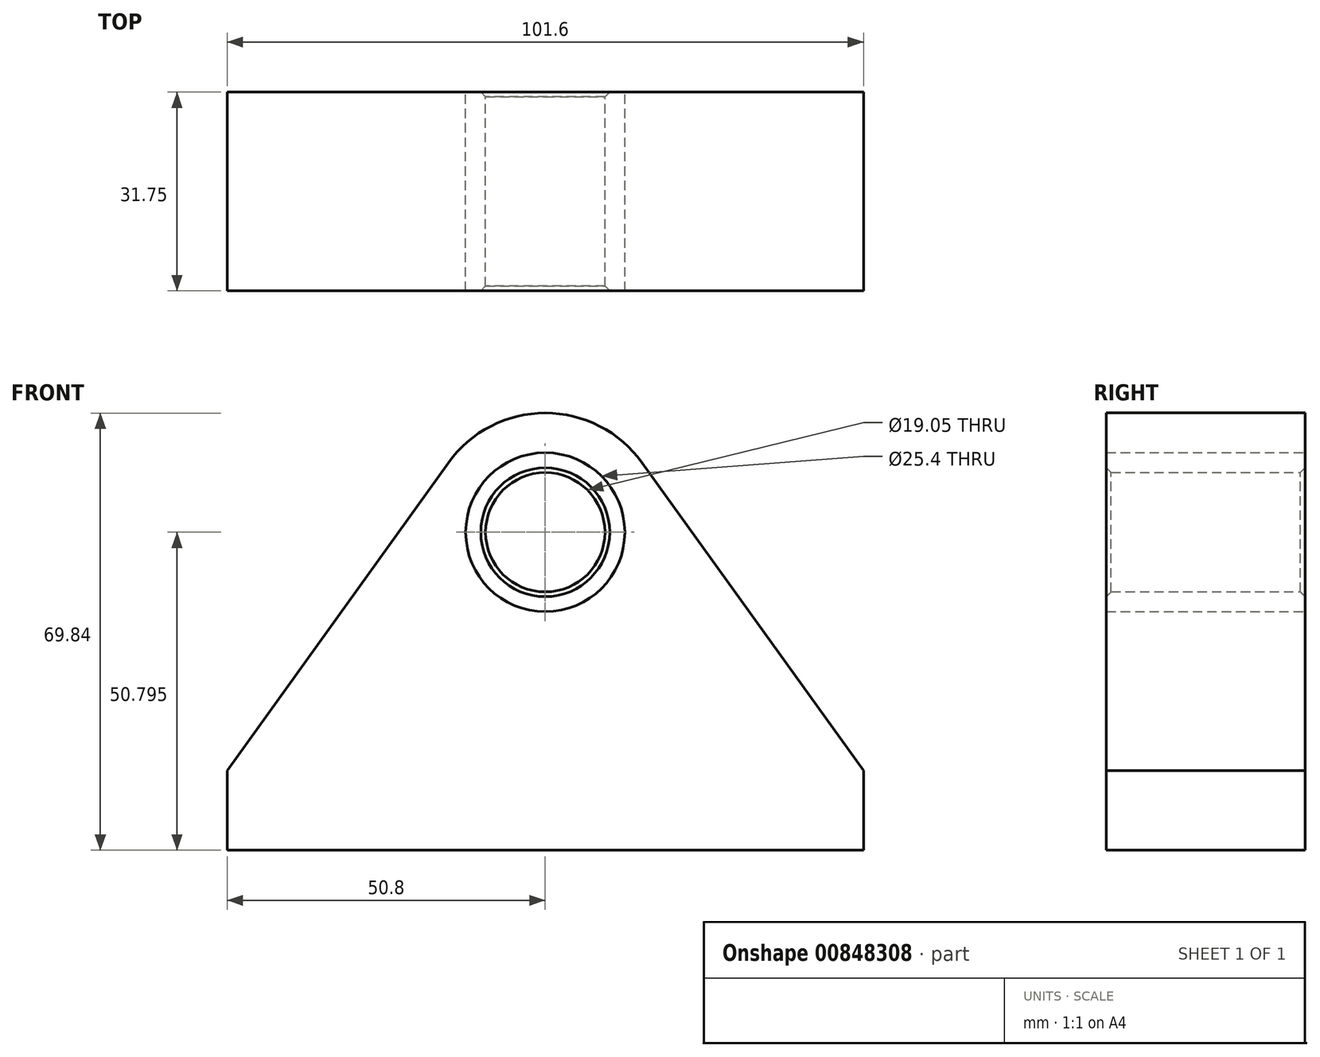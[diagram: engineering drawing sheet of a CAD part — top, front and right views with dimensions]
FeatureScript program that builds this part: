
annotation { "Feature Type Name" : "Feature", "Feature Type Description" : "" }
export const myFeature = defineFeature(function(context is Context, id is Id, definition is map)
    precondition{}
    {
        {
            var Q0;
            Q0=qCreatedBy(makeId("Front.planeOp"),FACE);
            var sketch = newSketch(context, id + "F0", { "sketchPlane" : qUnion([Q0])});
            skLineSegment(sketch, "E0.bottom", {"start": v(-50.8, -34.93) * mm, "end": v(50.8, -34.93) * mm});
            skLineSegment(sketch, "E0.left", {"start": v(-50.8, -34.93) * mm, "end": v(-50.8, -22.23) * mm});
            skLineSegment(sketch, "E0.right", {"start": v(50.8, -34.93) * mm, "end": v(50.8, -22.23) * mm});
            skPoint(sketch, "E0.middle", {"position": v(0, 0) * mm});
            skPoint(sketch, "E1", {"position": v(0, 15.87) * mm});
            skCircle(sketch, "E2", {"center": v(0, 15.87) * mm, "radius": 9.53 * mm});
            skPoint(sketch, "E3", {"position": v(-50.8, -22.23) * mm});
            skLineSegment(sketch, "E4", {"start": v(0, 34.93) * mm, "end": v(0, -34.93) * mm, "construction": true});
            skArc(sketch, "E5", {"start": v(15.48, 26.98) * mm, "mid": v(0, 34.93) * mm, "end": v(-15.48, 26.98) * mm});
            skLineSegment(sketch, "E6", {"start": v(-50.8, -22.23) * mm, "end": v(-15.48, 26.98) * mm});
            skLineSegment(sketch, "E7.MirrorCS", {"start": v(50.8, -22.23) * mm, "end": v(15.48, 26.98) * mm});
            skArc(sketch, "E8.MirrorCS", {"start": v(-15.48, 26.98) * mm, "mid": v(0, 34.93) * mm, "end": v(15.48, 26.98) * mm});
            skPoint(sketch, "E9.orphan", {"position": v(0, -3.18) * mm});
            skPoint(sketch, "E10.orphan", {"position": v(50.8, 34.93) * mm});
            skPoint(sketch, "E11.orphan", {"position": v(-50.8, 34.93) * mm});
            skCircle(sketch, "E12", {"center": v(0, 15.87) * mm, "radius": 12.7 * mm});
            skSolve(sketch);
        }
        {
            var Q0;
            Q0=makeQuery(id+"F0.imprint","IMPRINT",FACE,{"disambiguationData":[TD([[makeQuery(id+"F0.imprint","IMPRINT",EDGE,{"derivedFrom":sQuery(id+"F0.wireOp",EDGE,"E0.bottom")}),1.0]])]});
            extrude(context, id + "F1", {"entities" : qUnion([Q0]), "depth" : 31.75 * mm, "offsetDistance" : 25.4 * mm});
        }
        {
            var Q0;
            Q0=makeQuery(id+"F0.imprint","IMPRINT",FACE,{"disambiguationData":[TD([[makeQuery(id+"F0.imprint","IMPRINT",EDGE,{"derivedFrom":sQuery(id+"F0.wireOp",EDGE,"E2")}),-1.0]])]});
            extrude(context, id + "F2", {"entities" : qUnion([Q0]), "depth" : 31.75 * mm, "offsetDistance" : 25.4 * mm});
        }
        {
            var Q0;
            Q0=makeQuery(id+"F2.opExtrude","CAP_EDGE",EDGE,{"disambiguationData":[OSD([sQuery(id+"F0.wireOp",EDGE,"E2")])],"isStart":false});
            var Q1;
            Q1=makeQuery(id+"F2.opExtrude","CAP_EDGE",EDGE,{"disambiguationData":[OSD([sQuery(id+"F0.wireOp",EDGE,"E2")])],"isStart":true});
            chamfer(context, id + "F3", {"entities" : qUnion([Q0, Q1]), "width" : 0.76 * mm, "tangentPropagation" : true});
        }
    });
